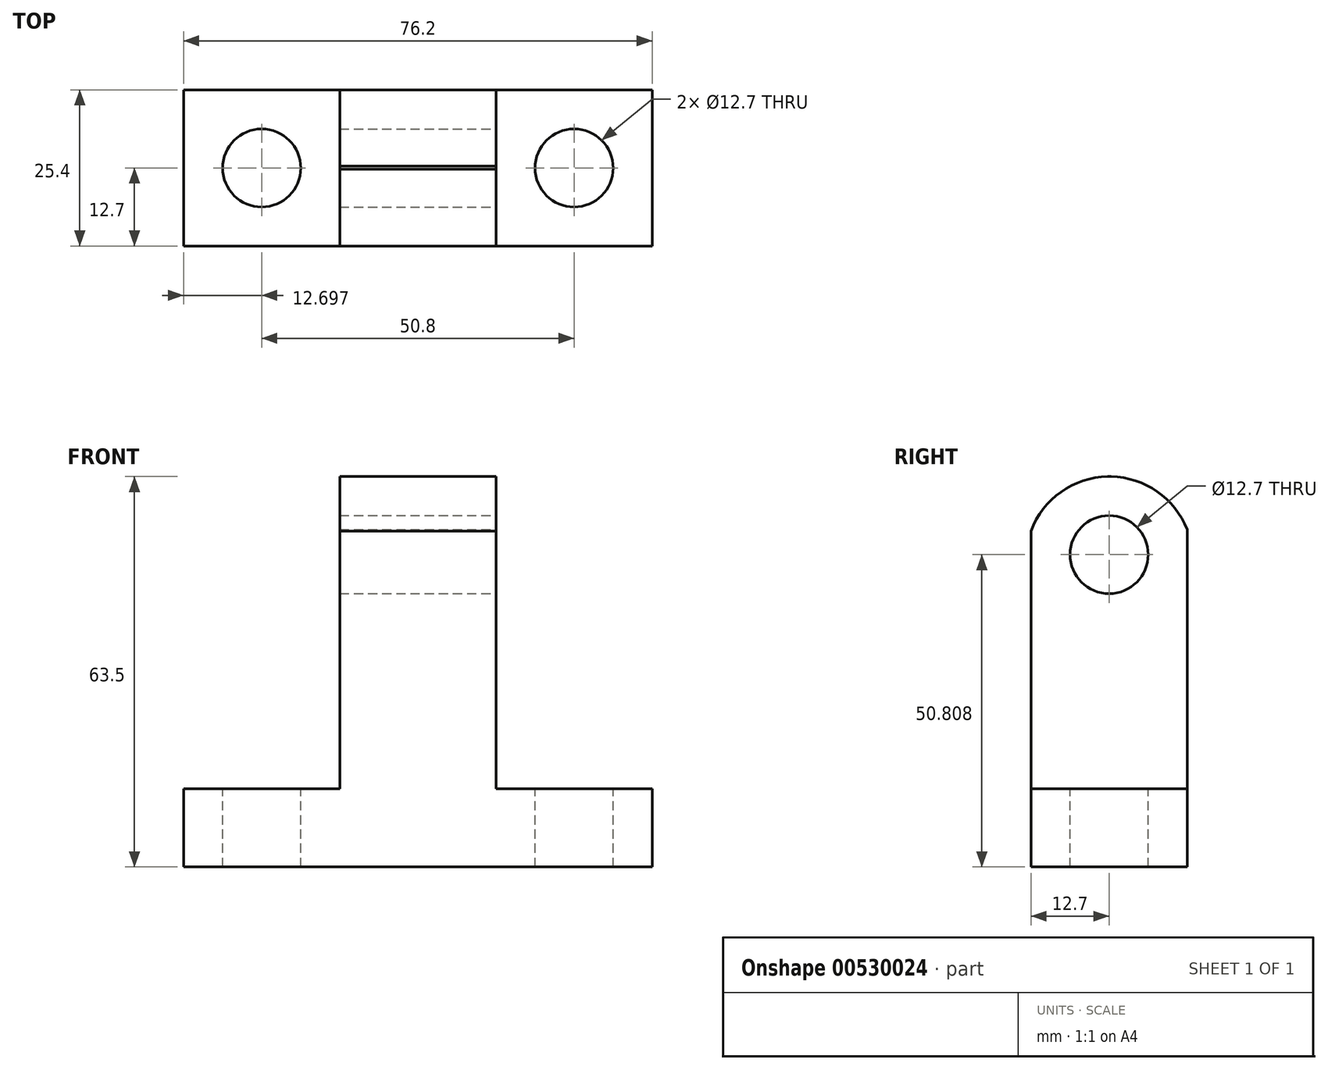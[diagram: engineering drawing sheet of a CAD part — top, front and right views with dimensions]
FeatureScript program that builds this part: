
annotation { "Feature Type Name" : "Feature", "Feature Type Description" : "" }
export const myFeature = defineFeature(function(context is Context, id is Id, definition is map)
    precondition{}
    {
        {
            var Q0;
            Q0=qCreatedBy(makeId("Front.planeOp"),FACE);
            var sketch = newSketch(context, id + "F0", { "sketchPlane" : qUnion([Q0])});
            skLineSegment(sketch, "E0", {"start": v(-68.86, 59.55) * mm, "end": v(-68.86, -3.95) * mm});
            skLineSegment(sketch, "E1", {"start": v(-68.86, -3.95) * mm, "end": v(7.34, -3.95) * mm});
            skLineSegment(sketch, "E2", {"start": v(7.34, -3.95) * mm, "end": v(7.34, 59.55) * mm});
            skLineSegment(sketch, "E3", {"start": v(-68.86, 59.55) * mm, "end": v(7.34, 59.55) * mm});
            skSolve(sketch);
        }
        {
            var Q0;
            Q0=makeQuery(id+"F0.imprint","IMPRINT",FACE,{"disambiguationData":[TD([[makeQuery(id+"F0.imprint","IMPRINT",EDGE,{"derivedFrom":sQuery(id+"F0.wireOp",EDGE,"E0")}),1.0]])]});
            extrude(context, id + "F1", {"entities" : qUnion([Q0]), "depth" : 25.4 * mm, "offsetDistance" : 25.4 * mm});
        }
        {
            var Q0;
            Q0=makeQuery(id+"F1.opExtrude","CAP_FACE",FACE,{"disambiguationData":[OSD([sQuery(id+"F0.wireOp",EDGE,"E0"),sQuery(id+"F0.wireOp",EDGE,"E1"),sQuery(id+"F0.wireOp",EDGE,"E2"),sQuery(id+"F0.wireOp",EDGE,"E3")])],"isStart":false});
            var sketch = newSketch(context, id + "F2", { "sketchPlane" : qUnion([Q0])});
            skLineSegment(sketch, "E4", {"start": v(-43.46, 59.55) * mm, "end": v(-43.46, 8.75) * mm});
            skLineSegment(sketch, "E5", {"start": v(-43.46, 8.75) * mm, "end": v(-68.86, 8.75) * mm});
            skLineSegment(sketch, "E6", {"start": v(-68.86, 8.75) * mm, "end": v(-68.86, 59.55) * mm});
            skLineSegment(sketch, "E7", {"start": v(-68.86, 59.55) * mm, "end": v(-43.46, 59.55) * mm});
            skLineSegment(sketch, "E8", {"start": v(-43.46, 59.55) * mm, "end": v(-18.06, 59.55) * mm});
            skLineSegment(sketch, "E9", {"start": v(-18.06, 59.55) * mm, "end": v(-18.06, 8.75) * mm});
            skLineSegment(sketch, "E10", {"start": v(-18.06, 8.75) * mm, "end": v(7.34, 8.75) * mm});
            skLineSegment(sketch, "E11", {"start": v(7.34, 8.75) * mm, "end": v(7.34, 59.55) * mm});
            skLineSegment(sketch, "E12", {"start": v(7.34, 59.55) * mm, "end": v(-18.06, 59.55) * mm});
            skSolve(sketch);
        }
        {
            var Q0;
            Q0=makeQuery(id+"F2.imprint","IMPRINT",FACE,{"disambiguationData":[TD([[makeQuery(id+"F2.imprint","IMPRINT",EDGE,{"derivedFrom":sQuery(id+"F2.wireOp",EDGE,"E4")}),-1.0]])]});
            var Q1;
            Q1=makeQuery(id+"F2.imprint","IMPRINT",FACE,{"disambiguationData":[TD([[makeQuery(id+"F2.imprint","IMPRINT",EDGE,{"derivedFrom":sQuery(id+"F2.wireOp",EDGE,"E9")}),1.0]])]});
            extrude(context, id + "F3", {"entities" : qUnion([Q0, Q1]), "operationType" : NewBodyOperationType.REMOVE, "endBound" : BoundingType.THROUGH_ALL, "oppositeDirection" : true, "depth" : 25.4 * mm, "offsetDistance" : 25.4 * mm});
        }
        {
            var Q0;
            Q0=makeQuery(id+"F3.boolean.opBoolean","COPY",FACE,{"derivedFrom":makeQuery(id+"F3.opExtrude","SWEPT_FACE",FACE,{"disambiguationData":[OSD([sQuery(id+"F2.wireOp",EDGE,"E5")])]})});
            var sketch = newSketch(context, id + "F4", { "sketchPlane" : qUnion([Q0])});
            skCircle(sketch, "E13", {"center": v(-56.16, -12.7) * mm, "radius": 6.35 * mm});
            skSolve(sketch);
        }
        {
            var Q0;
            Q0=makeQuery(id+"F3.boolean.opBoolean","COPY",FACE,{"derivedFrom":makeQuery(id+"F3.opExtrude","SWEPT_FACE",FACE,{"disambiguationData":[OSD([sQuery(id+"F2.wireOp",EDGE,"E10")])]})});
            var sketch = newSketch(context, id + "F5", { "sketchPlane" : qUnion([Q0])});
            skCircle(sketch, "E14", {"center": v(-5.36, -12.7) * mm, "radius": 6.35 * mm});
            skSolve(sketch);
        }
        {
            var Q0;
            Q0=makeQuery(id+"F3.boolean.opBoolean","COPY",FACE,{"derivedFrom":makeQuery(id+"F3.opExtrude","SWEPT_FACE",FACE,{"disambiguationData":[OSD([sQuery(id+"F2.wireOp",EDGE,"E9")])]})});
            var sketch = newSketch(context, id + "F6", { "sketchPlane" : qUnion([Q0])});
            skCircle(sketch, "E15", {"center": v(-12.7, 46.85) * mm, "radius": 6.35 * mm});
            skArc(sketch, "E16", {"start": v(0, 50.96) * mm, "mid": v(-12.79, 59.56) * mm, "end": v(-25.4, 50.7) * mm});
            skSolve(sketch);
        }
        {
            var Q0;
            {var subQ0=sQuery(id+"F6.wireOp",EDGE,"E16");var subQ1=sQuery(id+"F2.wireOp",EDGE,"E9");var subQ2=makeQuery(id+"F3.boolean.opBoolean","COPY",EDGE,{"derivedFrom":makeQuery(id+"F3.opExtrude","CAP_EDGE",EDGE,{"disambiguationData":[OSD([subQ1])],"isStart":true})});var subQ3=makeQuery(id+"F6.imprint","INTERSECT",VERTEX,{"derivedFrom":[subQ2,subQ0]});Q0=makeQuery(id+"F6.imprint","IMPRINT",FACE,{"disambiguationData":[TD([[makeQuery(id+"F6.imprint","IMPRINT",EDGE,{"disambiguationData":[TD([[subQ3,1.0]])],"derivedFrom":subQ0}),-1.0]])]});}
            var Q1;
            {var subQ0=sQuery(id+"F6.wireOp",EDGE,"E16");var subQ1=sQuery(id+"F2.wireOp",EDGE,"E9");var subQ4=makeQuery(id+"F3.boolean.opBoolean","COPY",EDGE,{"derivedFrom":makeQuery(id+"F3.opExtrude","SWEPT_EDGE",EDGE,{"disambiguationData":[OSD([sQuery(id+"F2.wireOp",EDGE,"E8"),subQ1,sQuery(id+"F2.wireOp",EDGE,"E12")])]})});var subQ5=makeQuery(id+"F6.imprint","INTERSECT",VERTEX,{"disambiguationData":[OD(0.0)],"derivedFrom":[subQ4,subQ0]});Q1=makeQuery(id+"F6.imprint","IMPRINT",FACE,{"disambiguationData":[TD([[makeQuery(id+"F6.imprint","IMPRINT",EDGE,{"disambiguationData":[TD([[subQ5,1.0]])],"derivedFrom":subQ0}),-1.0]])]});}
            extrude(context, id + "F7", {"entities" : qUnion([Q0, Q1]), "operationType" : NewBodyOperationType.REMOVE, "oppositeDirection" : true, "depth" : 25.4 * mm, "offsetDistance" : 25.4 * mm});
        }
        {
            var Q0;
            Q0=makeQuery(id+"F5.imprint","IMPRINT",FACE,{"disambiguationData":[TD([[makeQuery(id+"F5.imprint","IMPRINT",EDGE,{"derivedFrom":sQuery(id+"F5.wireOp",EDGE,"E14")}),1.0]])]});
            var Q1;
            Q1=makeQuery(id+"F4.imprint","IMPRINT",FACE,{"disambiguationData":[TD([[makeQuery(id+"F4.imprint","IMPRINT",EDGE,{"derivedFrom":sQuery(id+"F4.wireOp",EDGE,"E13")}),1.0]])]});
            extrude(context, id + "F8", {"entities" : qUnion([Q0, Q1]), "operationType" : NewBodyOperationType.REMOVE, "oppositeDirection" : true, "depth" : 25.4 * mm, "offsetDistance" : 25.4 * mm});
        }
        {
            var Q0;
            Q0=makeQuery(id+"F3.boolean.opBoolean","COPY",FACE,{"derivedFrom":makeQuery(id+"F3.opExtrude","SWEPT_FACE",FACE,{"disambiguationData":[OSD([sQuery(id+"F2.wireOp",EDGE,"E9")])]})});
            var sketch = newSketch(context, id + "F9", { "sketchPlane" : qUnion([Q0])});
            skCircle(sketch, "E17", {"center": v(-12.7, 46.86) * mm, "radius": 6.35 * mm});
            skSolve(sketch);
        }
        {
            var Q0;
            Q0=makeQuery(id+"F9.imprint","IMPRINT",FACE,{"disambiguationData":[TD([[makeQuery(id+"F9.imprint","IMPRINT",EDGE,{"derivedFrom":sQuery(id+"F9.wireOp",EDGE,"E17")}),1.0]])]});
            extrude(context, id + "F10", {"entities" : qUnion([Q0]), "operationType" : NewBodyOperationType.REMOVE, "endBound" : BoundingType.THROUGH_ALL, "oppositeDirection" : true, "depth" : 25.4 * mm, "offsetDistance" : 25.4 * mm});
        }
    });
